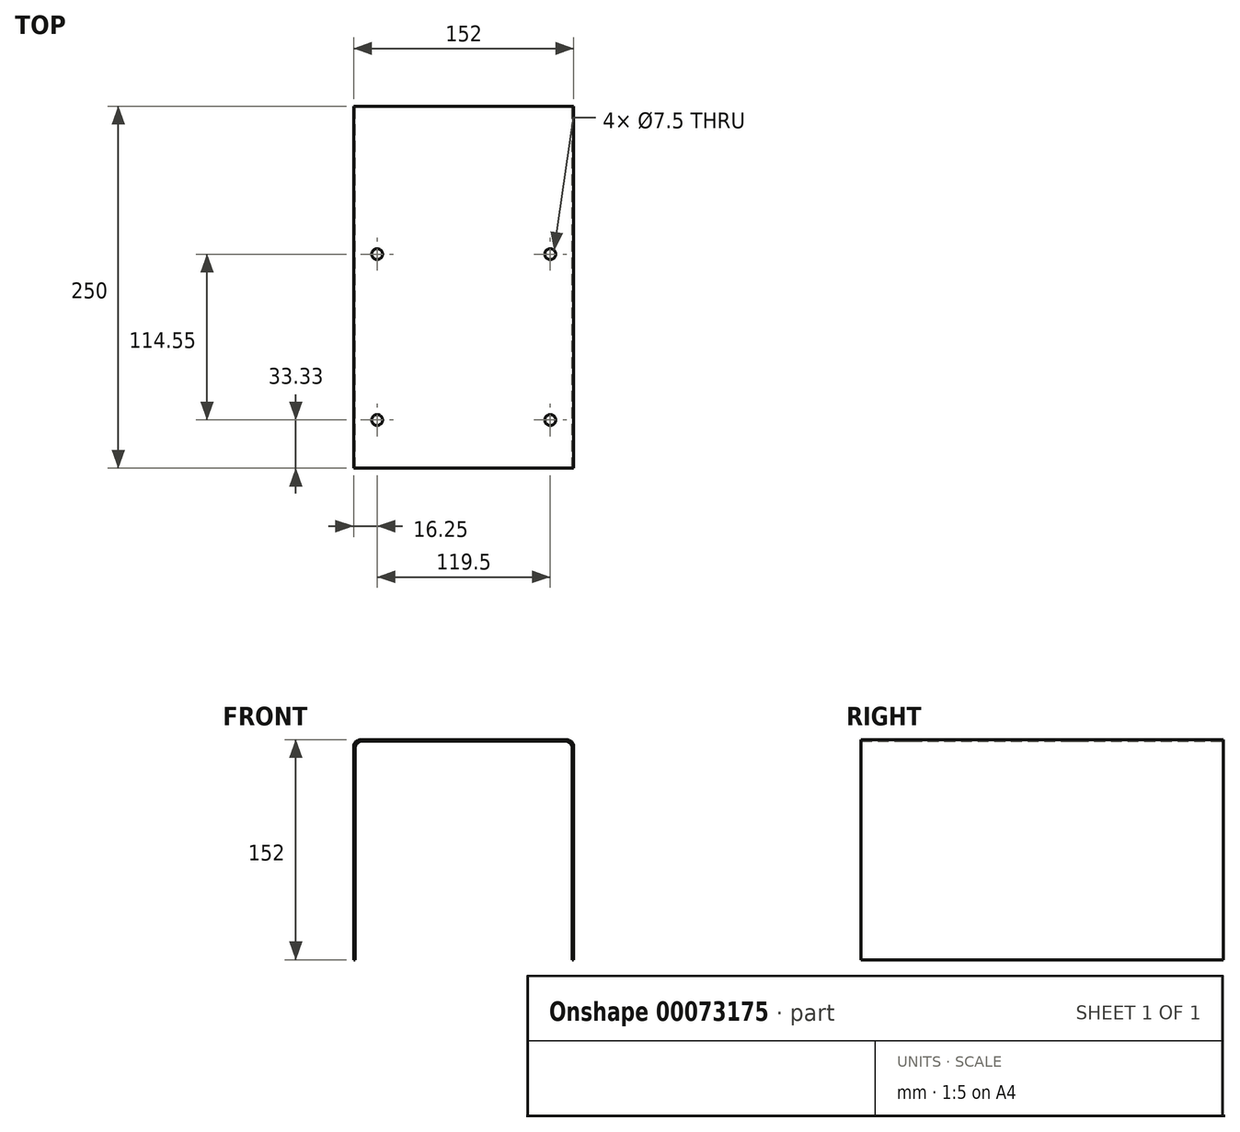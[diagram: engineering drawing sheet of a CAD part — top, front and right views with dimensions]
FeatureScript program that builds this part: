
annotation { "Feature Type Name" : "Feature", "Feature Type Description" : "" }
export const myFeature = defineFeature(function(context is Context, id is Id, definition is map)
    precondition{}
    {
        {
            var Q0;
            Q0=qCreatedBy(makeId("Front.planeOp"),FACE);
            var sketch = newSketch(context, id + "F0", { "sketchPlane" : qUnion([Q0])});
            skLineSegment(sketch, "E0", {"start": v(0, 76) * mm, "end": v(76, 76) * mm});
            skLineSegment(sketch, "E1", {"start": v(76, 76) * mm, "end": v(76, 0) * mm});
            skLineSegment(sketch, "E2.MirrorCS", {"start": v(0, 76) * mm, "end": v(-76, 76) * mm});
            skLineSegment(sketch, "E3.MirrorCS", {"start": v(-76, 76) * mm, "end": v(-76, 0) * mm});
            skLineSegment(sketch, "E4.MirrorCS", {"start": v(0, -76) * mm, "end": v(-76, -76) * mm});
            skLineSegment(sketch, "E5.MirrorCS", {"start": v(0, -76) * mm, "end": v(76, -76) * mm});
            skLineSegment(sketch, "E6.MirrorCS", {"start": v(76, -76) * mm, "end": v(76, 0) * mm});
            skLineSegment(sketch, "E7.MirrorCS", {"start": v(-76, -76) * mm, "end": v(-76, 0) * mm});
            skSolve(sketch);
        }
        {
            var Q0;
            Q0 = qSketchRegion(id + "F0", true);
            extrude(context, id + "F1", {"entities" : qUnion([Q0]), "endBound" : BoundingType.SYMMETRIC, "depth" : 250 * mm});
        }
        {
            var Q0;
            Q0=makeQuery(id+"F1.opExtrude","CAP_FACE",FACE,{"disambiguationData":[OSD([sQuery(id+"F0.wireOp",EDGE,"E0"),sQuery(id+"F0.wireOp",EDGE,"E1"),sQuery(id+"F0.wireOp",EDGE,"E2.MirrorCS"),sQuery(id+"F0.wireOp",EDGE,"E3.MirrorCS"),sQuery(id+"F0.wireOp",EDGE,"E4.MirrorCS"),sQuery(id+"F0.wireOp",EDGE,"E5.MirrorCS"),sQuery(id+"F0.wireOp",EDGE,"E6.MirrorCS"),sQuery(id+"F0.wireOp",EDGE,"E7.MirrorCS")])],"isStart":false});
            var Q1;
            Q1=makeQuery(id+"F1.opExtrude","SWEPT_FACE",FACE,{"disambiguationData":[OSD([sQuery(id+"F0.wireOp",EDGE,"E4.MirrorCS"),sQuery(id+"F0.wireOp",EDGE,"E5.MirrorCS")])]});
            var Q2;
            Q2=makeQuery(id+"F1.opExtrude","CAP_FACE",FACE,{"disambiguationData":[OSD([sQuery(id+"F0.wireOp",EDGE,"E0"),sQuery(id+"F0.wireOp",EDGE,"E1"),sQuery(id+"F0.wireOp",EDGE,"E2.MirrorCS"),sQuery(id+"F0.wireOp",EDGE,"E3.MirrorCS"),sQuery(id+"F0.wireOp",EDGE,"E4.MirrorCS"),sQuery(id+"F0.wireOp",EDGE,"E5.MirrorCS"),sQuery(id+"F0.wireOp",EDGE,"E6.MirrorCS"),sQuery(id+"F0.wireOp",EDGE,"E7.MirrorCS")])],"isStart":true});
            var Q3;
            Q3=makeQuery(id+"F1.opExtrude","SWEPT_BODY",BODY,{"disambiguationData":[OSD([sQuery(id+"F0.wireOp",EDGE,"E0"),sQuery(id+"F0.wireOp",EDGE,"E1"),sQuery(id+"F0.wireOp",EDGE,"E2.MirrorCS"),sQuery(id+"F0.wireOp",EDGE,"E3.MirrorCS"),sQuery(id+"F0.wireOp",EDGE,"E4.MirrorCS"),sQuery(id+"F0.wireOp",EDGE,"E5.MirrorCS"),sQuery(id+"F0.wireOp",EDGE,"E6.MirrorCS"),sQuery(id+"F0.wireOp",EDGE,"E7.MirrorCS")])]});
            shell(context, id + "F2", {"entities" : qUnion([Q0, Q1, Q2]), "parts" : qUnion([Q3]), "thickness" : 1 * mm});
        }
        {
            var Q0;
            Q0=makeQuery(id+"F1.opExtrude","SWEPT_FACE",FACE,{"disambiguationData":[OSD([sQuery(id+"F0.wireOp",EDGE,"E0"),sQuery(id+"F0.wireOp",EDGE,"E2.MirrorCS")])]});
            var sketch = newSketch(context, id + "F3", { "sketchPlane" : qUnion([Q0])});
            skLineSegment(sketch, "E8.rect.top", {"start": v(59.75, -91.67) * mm, "end": v(-59.75, -91.67) * mm});
            skPoint(sketch, "E8.rect.middle", {"position": v(0, 0) * mm});
            skLineSegment(sketch, "E9", {"start": v(-59.75, -91.67) * mm, "end": v(-59.75, 22.88) * mm});
            skLineSegment(sketch, "E10", {"start": v(-59.75, 22.88) * mm, "end": v(59.75, 22.88) * mm});
            skLineSegment(sketch, "E11", {"start": v(59.75, 22.88) * mm, "end": v(59.75, -91.67) * mm});
            skSolve(sketch);
        }
        {
            var Q0;
            Q0=sQuery(id+"F3.wireOp",VERTEX,"E10.start");
            var Q1;
            Q1=sQuery(id+"F3.wireOp",VERTEX,"E11.start");
            var Q2;
            Q2=sQuery(id+"F3.wireOp",VERTEX,"E11.end");
            var Q3;
            Q3=sQuery(id+"F3.wireOp",VERTEX,"E9.start");
            var Q4;
            Q4=makeQuery(id+"F1.opExtrude","SWEPT_BODY",BODY,{"disambiguationData":[OSD([sQuery(id+"F0.wireOp",EDGE,"E0"),sQuery(id+"F0.wireOp",EDGE,"E1"),sQuery(id+"F0.wireOp",EDGE,"E2.MirrorCS"),sQuery(id+"F0.wireOp",EDGE,"E3.MirrorCS"),sQuery(id+"F0.wireOp",EDGE,"E4.MirrorCS"),sQuery(id+"F0.wireOp",EDGE,"E5.MirrorCS"),sQuery(id+"F0.wireOp",EDGE,"E6.MirrorCS"),sQuery(id+"F0.wireOp",EDGE,"E7.MirrorCS")])]});
            hole(context, id + "F4", {"style" : HoleStyle.SIMPLE, "holeDiameter" : 7.5 * mm, "endStyle" : HoleEndStyle.THROUGH, "locations" : qUnion([Q0, Q1, Q2, Q3]), "scope" : qUnion([Q4]), "isTappedThrough" : true});
        }
        {
            var Q0;
            Q0=makeQuery(id+"F2.opShell","OFFSET_EDGE",EDGE,{"disambiguationData":[OSD([sQuery(id+"F0.wireOp",EDGE,"E2.MirrorCS"),sQuery(id+"F0.wireOp",EDGE,"E3.MirrorCS")])]});
            var Q1;
            Q1=makeQuery(id+"F2.opShell","OFFSET_EDGE",EDGE,{"disambiguationData":[OSD([sQuery(id+"F0.wireOp",EDGE,"E0"),sQuery(id+"F0.wireOp",EDGE,"E1")])]});
            var Q2;
            Q2=makeQuery(id+"F1.opExtrude","SWEPT_EDGE",EDGE,{"disambiguationData":[OSD([sQuery(id+"F0.wireOp",EDGE,"E0"),sQuery(id+"F0.wireOp",EDGE,"E1")])]});
            var Q3;
            Q3=makeQuery(id+"F1.opExtrude","SWEPT_EDGE",EDGE,{"disambiguationData":[OSD([sQuery(id+"F0.wireOp",EDGE,"E2.MirrorCS"),sQuery(id+"F0.wireOp",EDGE,"E3.MirrorCS")])]});
            fillet(context, id + "F5", {"entities" : qUnion([Q0, Q1, Q2, Q3]), "radius" : 5 * mm, "tangentPropagation" : true, "allowEdgeOverflow" : false});
        }
    });
